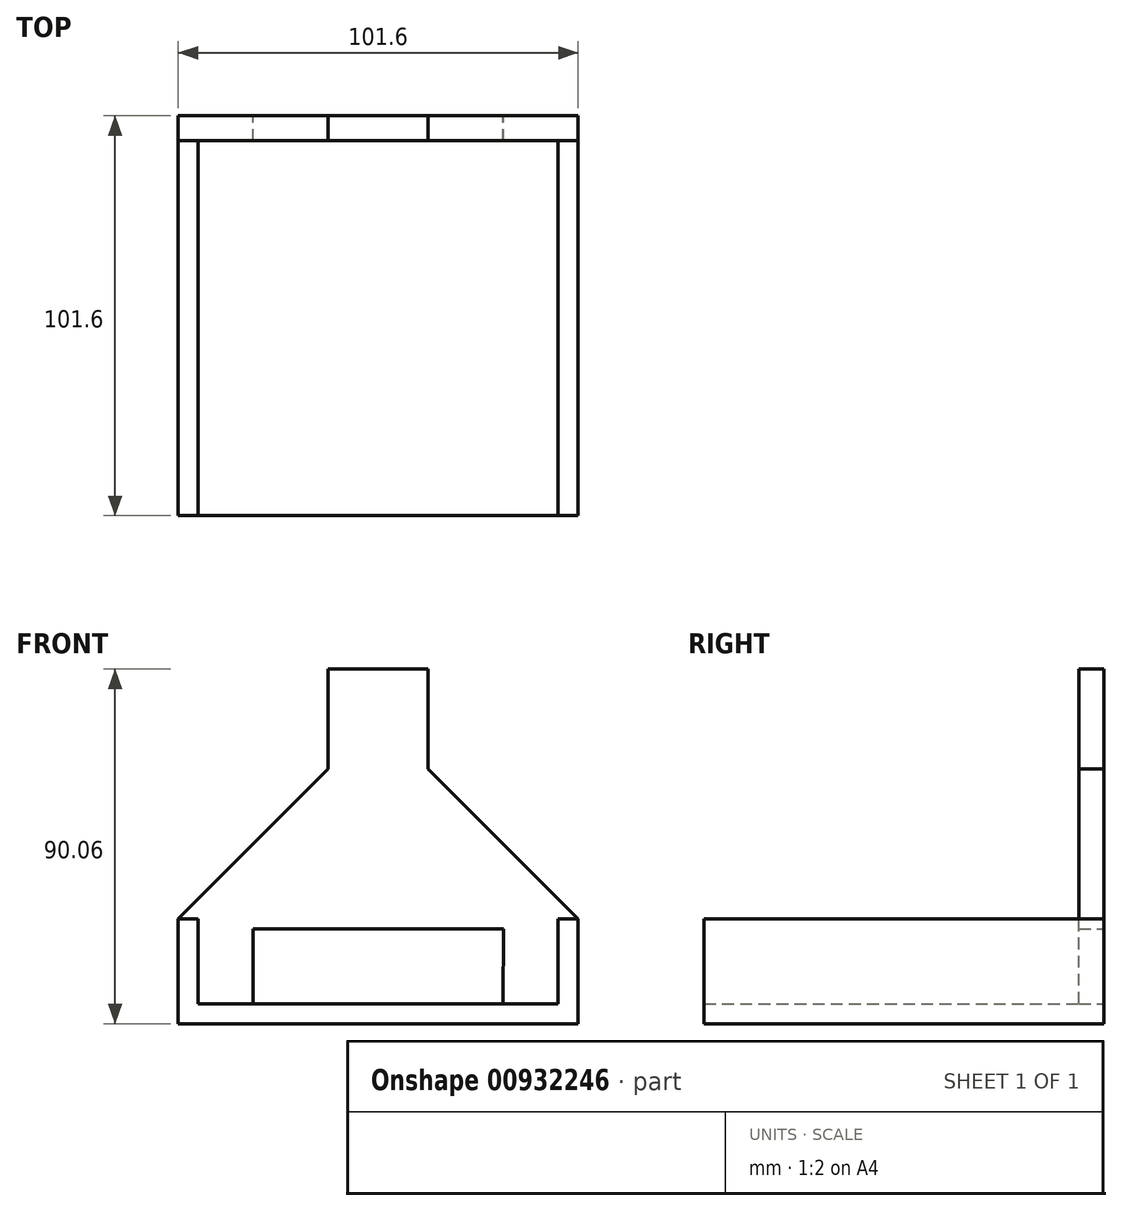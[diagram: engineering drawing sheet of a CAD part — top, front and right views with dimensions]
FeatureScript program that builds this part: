
annotation { "Feature Type Name" : "Feature", "Feature Type Description" : "" }
export const myFeature = defineFeature(function(context is Context, id is Id, definition is map)
    precondition{}
    {
        {
            var Q0;
            Q0=qCreatedBy(makeId("Front.planeOp"),FACE);
            var sketch = newSketch(context, id + "F0", { "sketchPlane" : qUnion([Q0])});
            skLineSegment(sketch, "E0", {"start": v(-50.8, -13.74) * mm, "end": v(50.8, -13.74) * mm});
            skLineSegment(sketch, "E1", {"start": v(-50.8, -13.74) * mm, "end": v(-50.8, 12.82) * mm});
            skLineSegment(sketch, "E2", {"start": v(-50.8, 12.82) * mm, "end": v(-45.72, 12.82) * mm});
            skLineSegment(sketch, "E3", {"start": v(-45.72, 12.82) * mm, "end": v(-45.72, -8.66) * mm});
            skLineSegment(sketch, "E4", {"start": v(-45.72, -8.66) * mm, "end": v(45.72, -8.66) * mm});
            skLineSegment(sketch, "E5", {"start": v(45.72, -8.66) * mm, "end": v(45.72, 12.82) * mm});
            skLineSegment(sketch, "E6", {"start": v(45.72, 12.82) * mm, "end": v(50.8, 12.82) * mm});
            skLineSegment(sketch, "E7", {"start": v(50.8, 12.82) * mm, "end": v(50.8, -13.74) * mm});
            skSolve(sketch);
        }
        {
            var Q0;
            Q0=makeQuery(id+"F0.imprint","IMPRINT",FACE,{"disambiguationData":[TD([[makeQuery(id+"F0.imprint","IMPRINT",EDGE,{"derivedFrom":sQuery(id+"F0.wireOp",EDGE,"E0")}),1.0]])]});
            extrude(context, id + "F1", {"entities" : qUnion([Q0]), "endBound" : BoundingType.SYMMETRIC, "depth" : 101.6 * mm, "offsetDistance" : 25.4 * mm});
        }
        {
            var Q0;
            Q0=makeQuery(id+"F1.opExtrude","CAP_FACE",FACE,{"disambiguationData":[OSD([sQuery(id+"F0.wireOp",EDGE,"E0"),sQuery(id+"F0.wireOp",EDGE,"E1"),sQuery(id+"F0.wireOp",EDGE,"E2"),sQuery(id+"F0.wireOp",EDGE,"E3"),sQuery(id+"F0.wireOp",EDGE,"E4"),sQuery(id+"F0.wireOp",EDGE,"E5"),sQuery(id+"F0.wireOp",EDGE,"E6"),sQuery(id+"F0.wireOp",EDGE,"E7")])],"isStart":true});
            var sketch = newSketch(context, id + "F2", { "sketchPlane" : qUnion([Q0])});
            skLineSegment(sketch, "E8.0", {"start": v(50.8, -13.74) * mm, "end": v(-50.8, -13.74) * mm});
            skLineSegment(sketch, "E9.0", {"start": v(-50.8, 12.82) * mm, "end": v(-50.8, -13.74) * mm});
            skLineSegment(sketch, "E10.0", {"start": v(50.8, -13.74) * mm, "end": v(50.8, 12.82) * mm});
            skLineSegment(sketch, "E11", {"start": v(-50.8, 12.82) * mm, "end": v(-12.7, 50.92) * mm});
            skLineSegment(sketch, "E12", {"start": v(-12.7, 50.92) * mm, "end": v(-12.7, 76.32) * mm});
            skLineSegment(sketch, "E13.MirrorCS", {"start": v(50.8, 12.82) * mm, "end": v(12.7, 50.92) * mm});
            skLineSegment(sketch, "E14.MirrorCS", {"start": v(12.7, 50.92) * mm, "end": v(12.7, 76.32) * mm});
            skLineSegment(sketch, "E15", {"start": v(-12.7, 76.32) * mm, "end": v(12.7, 76.32) * mm});
            skSolve(sketch);
        }
        {
            var Q0;
            Q0=makeQuery(id+"F2.imprint","IMPRINT",FACE,{"disambiguationData":[TD([[makeQuery(id+"F2.imprint","IMPRINT",EDGE,{"derivedFrom":sQuery(id+"F2.wireOp",EDGE,"E11")}),-1.0]])]});
            extrude(context, id + "F3", {"entities" : qUnion([Q0]), "operationType" : NewBodyOperationType.ADD, "oppositeDirection" : true, "depth" : 6.35 * mm, "offsetDistance" : 25.4 * mm});
        }
        {
            var Q0;
            {var subQ0=sQuery(id+"F0.wireOp",EDGE,"E6");var subQ1=sQuery(id+"F0.wireOp",EDGE,"E5");var subQ2=sQuery(id+"F0.wireOp",EDGE,"E4");var subQ3=sQuery(id+"F0.wireOp",EDGE,"E3");var subQ4=sQuery(id+"F0.wireOp",EDGE,"E2");Q0=makeQuery(id+"F3.boolean.opBoolean","MERGE",FACE,{"derivedFrom":[makeQuery(id+"F1.opExtrude","CAP_FACE",FACE,{"disambiguationData":[OSD([sQuery(id+"F0.wireOp",EDGE,"E0"),sQuery(id+"F0.wireOp",EDGE,"E1"),subQ4,subQ3,subQ2,subQ1,subQ0,sQuery(id+"F0.wireOp",EDGE,"E7")])],"isStart":true}),makeQuery(id+"F3.opExtrude","CAP_FACE",FACE,{"disambiguationData":[OSD([subQ4,subQ3,subQ2,subQ1,subQ0,sQuery(id+"F2.wireOp",EDGE,"E11"),sQuery(id+"F2.wireOp",EDGE,"E12"),sQuery(id+"F2.wireOp",EDGE,"E13.MirrorCS"),sQuery(id+"F2.wireOp",EDGE,"E14.MirrorCS"),sQuery(id+"F2.wireOp",EDGE,"E15")])],"isStart":true})]});}
            var sketch = newSketch(context, id + "F4", { "sketchPlane" : qUnion([Q0])});
            skLineSegment(sketch, "E16.0", {"start": v(31.75, -8.66) * mm, "end": v(-31.75, -8.66) * mm});
            skPoint(sketch, "E17.orphan", {"position": v(-45.72, -8.66) * mm});
            skPoint(sketch, "E18.orphan", {"position": v(45.72, -8.66) * mm});
            skLineSegment(sketch, "E19", {"start": v(31.75, 10.4) * mm, "end": v(31.75, -8.66) * mm});
            skLineSegment(sketch, "E20", {"start": v(31.75, 10.4) * mm, "end": v(-31.87, 10.4) * mm});
            skLineSegment(sketch, "E21", {"start": v(-31.87, 10.4) * mm, "end": v(-31.75, -8.66) * mm});
            skPoint(sketch, "E22.orphan", {"position": v(31.75, 12.82) * mm});
            skSolve(sketch);
        }
        {
            var Q0;
            Q0=makeQuery(id+"F4.imprint","IMPRINT",FACE,{"disambiguationData":[TD([[makeQuery(id+"F4.imprint","IMPRINT",EDGE,{"derivedFrom":sQuery(id+"F4.wireOp",EDGE,"E16.0")}),-1.0]])]});
            extrude(context, id + "F5", {"entities" : qUnion([Q0]), "operationType" : NewBodyOperationType.REMOVE, "endBound" : BoundingType.UP_TO_NEXT, "oppositeDirection" : true, "depth" : 25.4 * mm, "offsetDistance" : 25.4 * mm});
        }
    });
